# Revit family: IS_Conca_BD460_BIM_DE
name_source: partatom
category: Plumbing Fixtures
units: mm (PartAtom-declared; Revit-internal decimal feet)

## family parameters
Always vertical = No
Cut with Voids When Loaded = No
OmniClass Number = 23.45.55.17
OmniClass Title = Mixing Faucets
Part Type = Normal
Room Calculation Point = No
Round Connector Dimension = Use Diameter
Shared = No
Work Plane-Based = No

## types (4) — shared parameters
Accessories = https://www.idealstandard.de
Afmetingen = 130 x 299 x 875 mm
AreaUnits = Millimetres
AssetType = Fixed
Auteur = Ideal Standard GmbH
BIMObjectName = IS_IdealStandard_Bathmanualwatersupplysets_Conca_BD460
BIMobject category = Taps & Mixers
BIMobject category code = sanitary-taps-mixers
BIMobject main category = Sanitary
BIMobject main category code = sanitary
Beschrijvinggarantie = Garantie van de fabrikant
BimObjectNaam = IS_IdealStandard_Bathmanualwatersupplysets_Conca_BD460
Brand = Ideal Standard
Brand url = https://www.idealstandard.de
Breedte = 130.02034
Category = Sanitary
Classification = Bath and Shower Mixer
ConnectionType = plumbing
CurrencyUnit = €
CurrentRevision = 1
Date of publishing = 23/06/2023
Description = Conca Freestanding Bath & Shower Mixer Kit 2 and Shower Set
Douchebak = No
DurationUnit = Years
DuurEenheid = Jaar
Edition number = 1
ElementType = Bath & Shower Mixer
FaucetFunction = Bath & Shower Mixer
FaucetOperation = Sinlge Level
FaucetTopDescription = Sinlge Level Bath & Shower Mixer
FaucetType = Sinlge Level Bath & Shower Mixer
Features = Freestanding Bath & Shower Mixer Kit 2 and Shower Set
Garantieonderdelen = 5
Garantieunits = Jaar
Help = https://www.idealstandard.de
Hoogte = 874,976257511414
Hulp = https://www.idealstandard.de
IFC Classification = Sanitary Terminal
IfcExportAs = IfcValveType
IfcExportType = FAUCET
Installatieinstructies = https://www.idealstandard.de
Installation instructions = https://www.idealstandard.de
InstallationInstructions = https://www.idealstandard.de
Lengte = 299 mm
LinearUnits = Millimetres
MaintenanceInformation = https://www.idealstandard.de
Manufacturer = Ideal Standard
Manufacturer name = Ideal Standard
ManufacturerURL = https://www.idealstandard.de
Materiaal = messing
Material = Brass
Material main = Brass
Merk = Ideal Standard GmbH
ModelReference = Conca Freestanding Bath & Shower Mixer Kit 2 and Shower Set
NBS Reference Code = 35-06-07
NBS Reference Description = Bath Water Supply Fittings
Name = Bathmanualwatersupplysets_Conca_BD460_IdealStandard
NettWeight = 8,247
NominalDepth = 299 mm
NominalHeight = 875 mm
NominalLength = 299 mm
NominalWidth = 130 mm  [stored 0.426509 ft]
OmniClass Code = 23-31 11 00
OmniClass Description = Faucets
OppervlakteEenheid = millimeter
PredefinedType = Faucets
Product Guid = d97d23a1-f7e7-4ae3-acc8-d77d0ec415a5
Product SKU = BD460
Product certification = https://www.idealstandard.de
Product data url = https://bimobject.com
Product family = CONCA
Product group = Taps & Mixers
Product name = Conca Freestanding Bath & Shower Mixer Kit 2 and Shower Set
Product url = https://www.idealstandard.de
ProductInformation = https://www.idealstandard.de
Productinformatie = https://www.idealstandard.de
QR code = http://bimobject.com
Revisie = 1
Shape = Cylindrical
ShowerType = Free Standaing Bath and Shower Mixer
Size = 130 x 299 x 875 mm
Space = Internal
SpareParts = https://www.idealstandard.de
Technical description = https://www.idealstandard.de
Telefoonnummer = +49 (0) 228 521 0
TestPressure = 10 Bar
Typeconnectie = Loodgieter
UNSPSC Code = 301815
URL = https://www.idealstandard.de
Uniclass 1.4 Code = L725111
Uniclass 1.4 Description = Mixer taps
Uniclass 2.0 Code = PR-35-06-07
Uniclass 2.0 Description = Bath Water Supply Fittings
Uniclass 2015 Code = Pr_40_20_87_07
Uniclass 2015 Name = Bath manual water supply sets
Uniclass2015Beschrijving = Bath manual water supply sets
Uniclass2015Code = Pr_40_20_87_07
Uniclass2015Referentie = Pr_40_20_87_07
Uniclass2015Title = Bath manual water supply sets
Uniclass2015Version = v1.25
Urlproducent = https://www.idealstandard.de
ValutaEenheid = €
Versie = 1
Version = 1
Verwachtelevensduur = 30
VolumeUnits = litres
Volumeunits = Liter
Vorm = Cilindrisch
WRASURL = https://www.wrasapprovals.co.uk
WarrantyDescription = manufacturer warranty
WarrantyDurationParts = 5
WarrantyDurationUnit = Years
WarrantyGuarantorParts = https://www.idealstandard.de
Wisselstukken = https://www.idealstandard.de
Youtube clip = https://www.youtube.com
zero-valued in all types: BrutoGewicht, Cost, Default Elevation, Diepte, Nettogewicht, Vervangingskosten

## per-type parameters (varying)
| type | Afwerking | Artikelnummer | Artikelomschrijving | Artikelreferentie | BarCode | Barcode | Color | Eigenschappen | Finish | GTIN code | Kleur | MainColor | Model | ModelNumber | Referentie |
| BD460A2 - Conca Freestanding Bath & Shower Mixer Kit 2 and Shower Set - Brushed Gold | Brushed gold | BD460A2 | Conca freistehender Badewannen- und Duschmischer-Kit 2 und Duschset - Gebürstetes Gold | Conca freistehender Badewannen- und Duschmischer-Kit 2 und Duschset - Gebürstetes Gold | 3800861110804 | 3800861110804 | Brushed Gold | Conca Freestanding Bath & Shower Mixer Kit 2 and Shower Set - Brushed Gold | Brushed Gold | https://3800861110804 | Brushed gold | Brushed Gold | BD460A2 | BD460A2 | Conca freistehender Badewannen- und Duschmischer-Kit 2 und Duschset - Gebürstetes Gold |
| BD460A5 - Conca Freestanding Bath & Shower Mixer Kit 2 and Shower Set - Magnetic Grey | Brushed Gun metal | BD460A5 | Conca freistehender Badewannen- und Duschmischer-Kit 2 und Duschset - Magnetgrau | Conca freistehender Badewannen- und Duschmischer-Kit 2 und Duschset - Magnetgrau | 3800861110910 | 3800861110910 | Magnetic Grey | Conca Freestanding Bath & Shower Mixer Kit 2 and Shower Set - Magnetic Grey | Magnetic Grey | https://3800861110910 | Brushed Gun metal | Magnetic Grey | BD460A5 | BD460A5 | Conca freistehender Badewannen- und Duschmischer-Kit 2 und Duschset - Magnetgrau |
| BD460AA - Conca Freestanding Bath & Shower Mixer Kit 2 and Shower Set - Chrome | Chrome | BD460AA | Conca freistehender Badewannen- und Duschmischer-Kit 2 und Duschset - Chrom | Conca freistehender Badewannen- und Duschmischer-Kit 2 und Duschset - Chrom | 3800861110699 | 3800861110699 | Chrome | Conca Freestanding Bath & Shower Mixer Kit 2 and Shower Set - Chrome | Chrome | https://3800861110699 | Chrome | Chrome | BD460AA | BD460AA | Conca freistehender Badewannen- und Duschmischer-Kit 2 und Duschset - Chrom |
| BD460GN - Conca Freestanding Bath & Shower Mixer Kit 2 and Shower Set - Silver Storm | Brushed nickel | BD460GN | Conca freistehender Badewannen- und Duschmischer-Kit 2 und Duschset - Silbersturm | Conca freistehender Badewannen- und Duschmischer-Kit 2 und Duschset - Silbersturm | 3800861111023 | 3800861111023 | Silver Storm | Conca Freestanding Bath & Shower Mixer Kit 2 and Shower Set - Silver Storm | Silver Storm | https://3800861111023 | Brushed nickel | Silver Storm | BD460GN | BD460GN | Conca freistehender Badewannen- und Duschmischer-Kit 2 und Duschset - Silbersturm |

note: [stored X ft] marks values corroborated as IEEE doubles in the binary element streams (Revit-internal decimal feet)

## geometry (parser evidence)
native form markers: Blend x2, Sweep x3
no freeform markers — native parametric forms only
